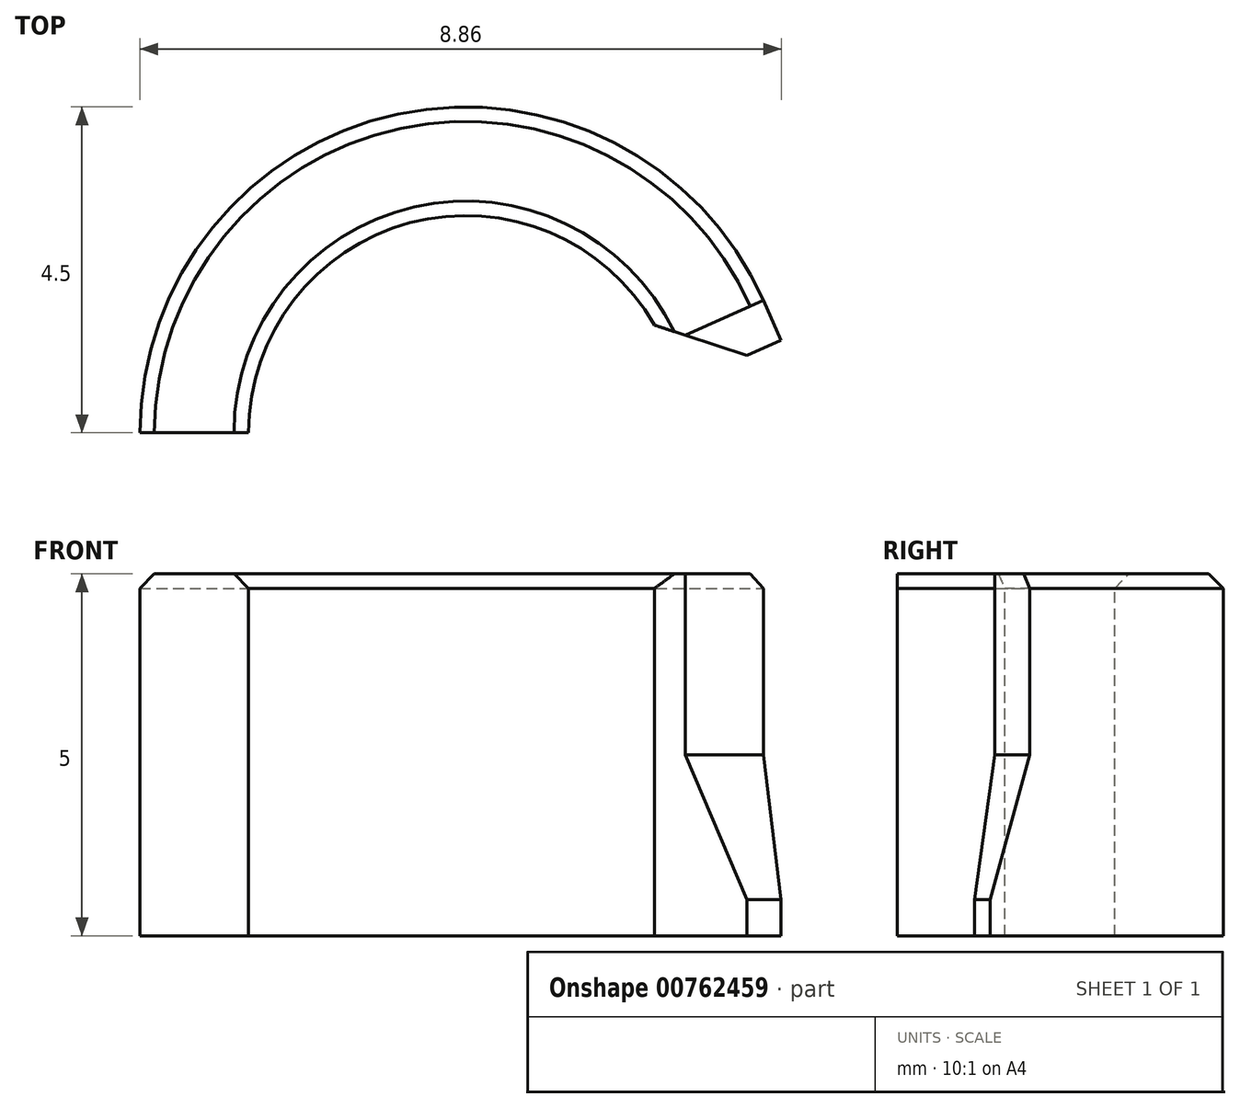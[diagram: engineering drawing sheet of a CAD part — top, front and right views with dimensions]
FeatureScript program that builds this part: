
annotation { "Feature Type Name" : "Feature", "Feature Type Description" : "" }
export const myFeature = defineFeature(function(context is Context, id is Id, definition is map)
    precondition{}
    {
        {
            var Q0;
            Q0=qCreatedBy(makeId("Top.planeOp"),FACE);
            var sketch = newSketch(context, id + "F0", { "sketchPlane" : qUnion([Q0])});
            skArc(sketch, "E0", {"start": v(4.11, 1.83) * mm, "mid": v(-0.93, 4.4) * mm, "end": v(-4.5, 0) * mm});
            skArc(sketch, "E1", {"start": v(2.74, 1.22) * mm, "mid": v(-0.62, 2.93) * mm, "end": v(-3, 0) * mm});
            skLineSegment(sketch, "E2", {"start": v(-4.5, 0) * mm, "end": v(-3, 0) * mm});
            skLineSegment(sketch, "E3", {"start": v(2.74, 1.22) * mm, "end": v(4.11, 1.83) * mm});
            skSolve(sketch);
        }
        {
            var Q0;
            Q0=makeQuery(id+"F0.imprint","IMPRINT",FACE,{"disambiguationData":[TD([[makeQuery(id+"F0.imprint","IMPRINT",EDGE,{"derivedFrom":sQuery(id+"F0.wireOp",EDGE,"E0")}),1.0]])]});
            extrude(context, id + "F1", {"entities" : qUnion([Q0]), "depth" : 5 * mm, "offsetDistance" : 25 * mm});
        }
        {
            var Q0;
            Q0=makeQuery(id+"F1.opExtrude","SWEPT_FACE",FACE,{"disambiguationData":[OSD([sQuery(id+"F0.wireOp",EDGE,"E3")])]});
            var sketch = newSketch(context, id + "F2", { "sketchPlane" : qUnion([Q0])});
            skLineSegment(sketch, "E4", {"start": v(4.5, 5) * mm, "end": v(4.5, 2.5) * mm});
            skLineSegment(sketch, "E5", {"start": v(4.5, 2.5) * mm, "end": v(3, 2.5) * mm});
            skLineSegment(sketch, "E6", {"start": v(3, 2.5) * mm, "end": v(3, 5) * mm});
            skLineSegment(sketch, "E7", {"start": v(3, 5) * mm, "end": v(4.5, 5) * mm});
            skSolve(sketch);
        }
        {
            var Q0;
            Q0=makeQuery(id+"F2.imprint","IMPRINT",FACE,{"disambiguationData":[TD([[makeQuery(id+"F2.imprint","IMPRINT",EDGE,{"derivedFrom":sQuery(id+"F2.wireOp",EDGE,"E4")}),-1.0]])]});
            extrude(context, id + "F3", {"entities" : qUnion([Q0]), "operationType" : NewBodyOperationType.ADD, "depth" : 0.6 * mm, "offsetDistance" : 25 * mm});
        }
        {
            var Q0;
            Q0=makeQuery(id+"F3.opExtrude","CAP_EDGE",EDGE,{"disambiguationData":[OSD([sQuery(id+"F2.wireOp",EDGE,"E5")])],"isStart":false});
            chamfer(context, id + "F4", {"entities" : qUnion([Q0]), "chamferType" : ChamferType.TWO_OFFSETS, "width1" : 0.6 * mm, "oppositeDirection" : false, "width2" : 2 * mm, "tangentPropagation" : true});
        }
        {
            var Q0;
            Q0=makeQuery(id+"F3.opExtrude","CAP_EDGE",EDGE,{"disambiguationData":[OSD([sQuery(id+"F2.wireOp",EDGE,"E6")])],"isStart":false});
            chamfer(context, id + "F5", {"entities" : qUnion([Q0]), "width" : 1 * mm});
        }
        {
            var Q0;
            Q0=makeQuery(id+"F1.opExtrude","SWEPT_BODY",BODY,{"disambiguationData":[OSD([sQuery(id+"F0.wireOp",EDGE,"E0"),sQuery(id+"F0.wireOp",EDGE,"E1"),sQuery(id+"F0.wireOp",EDGE,"E2"),sQuery(id+"F0.wireOp",EDGE,"E3")])]});
            var Q1;
            Q1=makeQuery(id+"F1.opExtrude","CAP_FACE",FACE,{"disambiguationData":[OSD([sQuery(id+"F0.wireOp",EDGE,"E0"),sQuery(id+"F0.wireOp",EDGE,"E1"),sQuery(id+"F0.wireOp",EDGE,"E2"),sQuery(id+"F0.wireOp",EDGE,"E3")])],"isStart":true});
            mirror(context, id + "F6", {"entities" : qUnion([Q0]), "mirrorPlane" : qUnion([Q1])});
        }
        {
            var Q0;
            Q0=makeQuery(id+"F1.opExtrude","SWEPT_BODY",BODY,{"disambiguationData":[OSD([sQuery(id+"F0.wireOp",EDGE,"E0"),sQuery(id+"F0.wireOp",EDGE,"E1"),sQuery(id+"F0.wireOp",EDGE,"E2"),sQuery(id+"F0.wireOp",EDGE,"E3")])]});
            deleteBodies(context, id + "F7", {"entities" : qUnion([Q0])});
        }
        {
            var Q0;
            Q0=makeQuery(id+"F6.opPattern","COPY",EDGE,{"derivedFrom":makeQuery(id+"F1.opExtrude","CAP_EDGE",EDGE,{"disambiguationData":[OSD([sQuery(id+"F0.wireOp",EDGE,"E1")])],"isStart":true}),"instanceName":"1"});
            var Q1;
            Q1=makeQuery(id+"F6.opPattern","COPY",EDGE,{"derivedFrom":makeQuery(id+"F1.opExtrude","CAP_EDGE",EDGE,{"disambiguationData":[OSD([sQuery(id+"F0.wireOp",EDGE,"E0")])],"isStart":true}),"instanceName":"1"});
            chamfer(context, id + "F8", {"entities" : qUnion([Q0, Q1]), "width" : 0.2 * mm, "tangentPropagation" : true});
        }
    });
